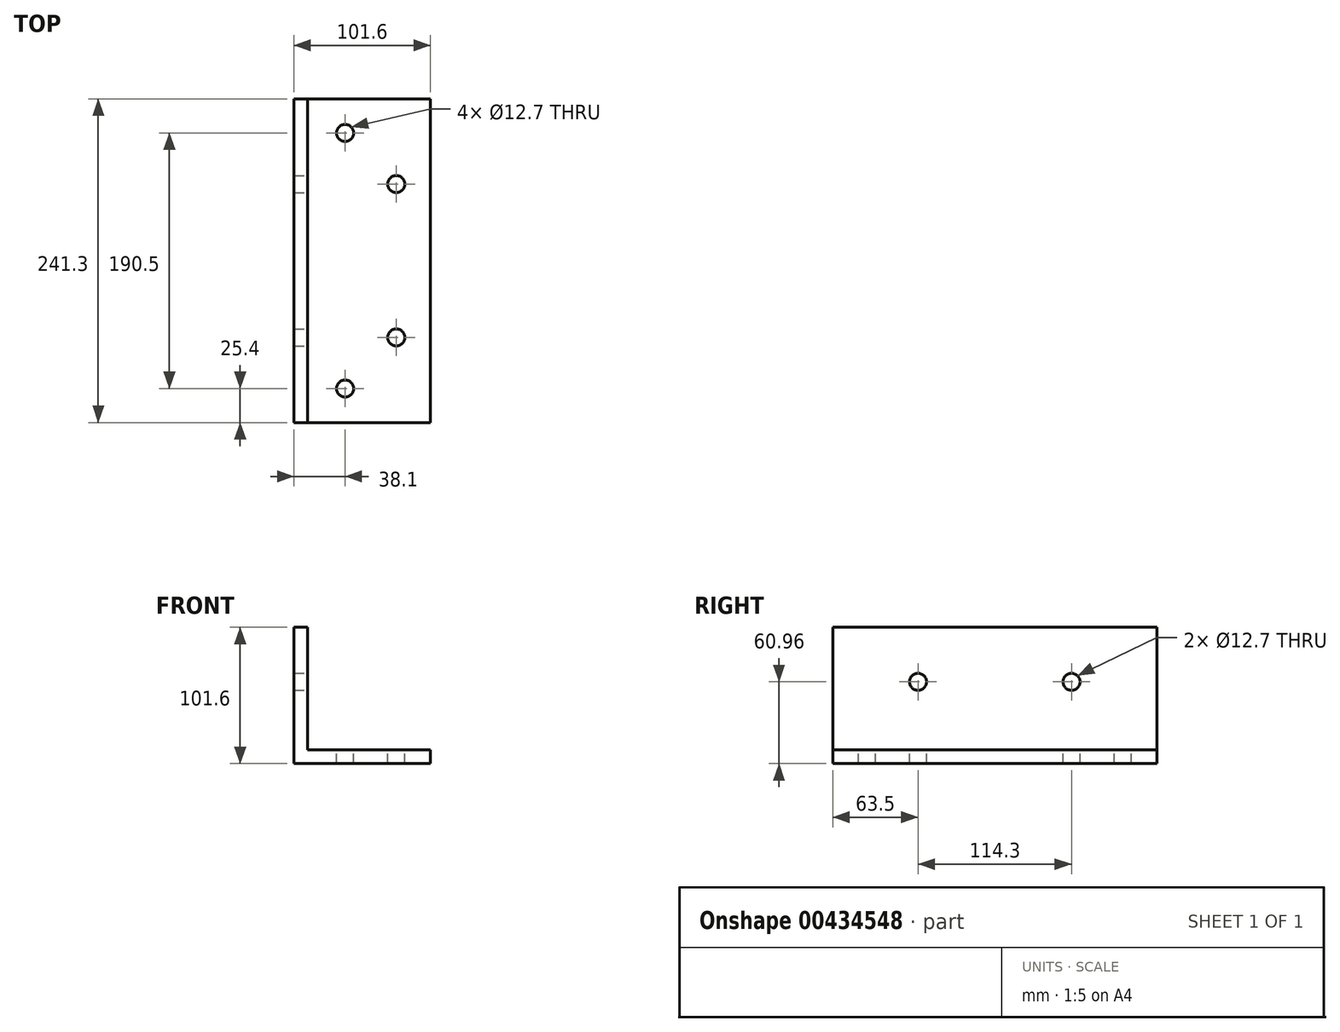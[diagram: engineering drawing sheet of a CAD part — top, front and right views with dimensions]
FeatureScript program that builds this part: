
annotation { "Feature Type Name" : "Feature", "Feature Type Description" : "" }
export const myFeature = defineFeature(function(context is Context, id is Id, definition is map)
    precondition{}
    {
        {
            var Q0;
            Q0=qCreatedBy(makeId("Front.planeOp"),FACE);
            var sketch = newSketch(context, id + "F0", { "sketchPlane" : qUnion([Q0])});
            skLineSegment(sketch, "E0.bottom", {"start": v(0, 0) * mm, "end": v(-10.16, 0) * mm});
            skLineSegment(sketch, "E0.top", {"start": v(0, 101.6) * mm, "end": v(-10.16, 101.6) * mm});
            skLineSegment(sketch, "E0.left", {"start": v(0, 10.16) * mm, "end": v(0, 101.6) * mm});
            skLineSegment(sketch, "E0.right", {"start": v(-10.16, 0) * mm, "end": v(-10.16, 101.6) * mm});
            skLineSegment(sketch, "E1.bottom", {"start": v(-10.16, 0) * mm, "end": v(91.44, 0) * mm});
            skLineSegment(sketch, "E1.top", {"start": v(0, 10.16) * mm, "end": v(91.44, 10.16) * mm});
            skLineSegment(sketch, "E1.left", {"start": v(-10.16, 0) * mm, "end": v(-10.16, 10.16) * mm});
            skLineSegment(sketch, "E1.right", {"start": v(91.44, 0) * mm, "end": v(91.44, 10.16) * mm});
            skSolve(sketch);
        }
        {
            var Q0;
            Q0 = qSketchRegion(id + "F0", true);
            extrude(context, id + "F1", {"entities" : qUnion([Q0]), "depth" : 241.3 * mm});
        }
        {
            var Q0;
            Q0=makeQuery(id+"F1.opExtrude","SWEPT_FACE",FACE,{"disambiguationData":[OSD([sQuery(id+"F0.wireOp",EDGE,"E1.top")])]});
            var sketch = newSketch(context, id + "F2", { "sketchPlane" : qUnion([Q0])});
            skCircle(sketch, "E2", {"center": v(66.04, -177.8) * mm, "radius": 6.35 * mm});
            skCircle(sketch, "E3", {"center": v(66.04, -63.5) * mm, "radius": 6.35 * mm});
            skCircle(sketch, "E4", {"center": v(27.94, -215.9) * mm, "radius": 6.35 * mm});
            skCircle(sketch, "E5", {"center": v(27.94, -25.4) * mm, "radius": 6.35 * mm});
            skSolve(sketch);
        }
        {
            var Q0;
            Q0=makeQuery(id+"F2.imprint","IMPRINT",FACE,{"disambiguationData":[TD([[makeQuery(id+"F2.imprint","IMPRINT",EDGE,{"derivedFrom":sQuery(id+"F2.wireOp",EDGE,"E5")}),1.0]])]});
            var Q1;
            Q1=makeQuery(id+"F2.imprint","IMPRINT",FACE,{"disambiguationData":[TD([[makeQuery(id+"F2.imprint","IMPRINT",EDGE,{"derivedFrom":sQuery(id+"F2.wireOp",EDGE,"E3")}),1.0]])]});
            var Q2;
            Q2=makeQuery(id+"F2.imprint","IMPRINT",FACE,{"disambiguationData":[TD([[makeQuery(id+"F2.imprint","IMPRINT",EDGE,{"derivedFrom":sQuery(id+"F2.wireOp",EDGE,"E2")}),1.0]])]});
            var Q3;
            Q3=makeQuery(id+"F2.imprint","IMPRINT",FACE,{"disambiguationData":[TD([[makeQuery(id+"F2.imprint","IMPRINT",EDGE,{"derivedFrom":sQuery(id+"F2.wireOp",EDGE,"E4")}),1.0]])]});
            extrude(context, id + "F3", {"entities" : qUnion([Q0, Q1, Q2, Q3]), "operationType" : NewBodyOperationType.REMOVE, "oppositeDirection" : true, "depth" : 50.8 * mm});
        }
        {
            var Q0;
            Q0=makeQuery(id+"F1.opExtrude","SWEPT_FACE",FACE,{"disambiguationData":[OSD([sQuery(id+"F0.wireOp",EDGE,"E0.left")])]});
            var sketch = newSketch(context, id + "F4", { "sketchPlane" : qUnion([Q0])});
            skCircle(sketch, "E6", {"center": v(-177.8, 60.96) * mm, "radius": 6.35 * mm});
            skCircle(sketch, "E7", {"center": v(-63.5, 60.96) * mm, "radius": 6.35 * mm});
            skSolve(sketch);
        }
        {
            var Q0;
            Q0 = qSketchRegion(id + "F4", true);
            extrude(context, id + "F5", {"entities" : qUnion([Q0]), "operationType" : NewBodyOperationType.REMOVE, "oppositeDirection" : true, "depth" : 25.4 * mm});
        }
    });
